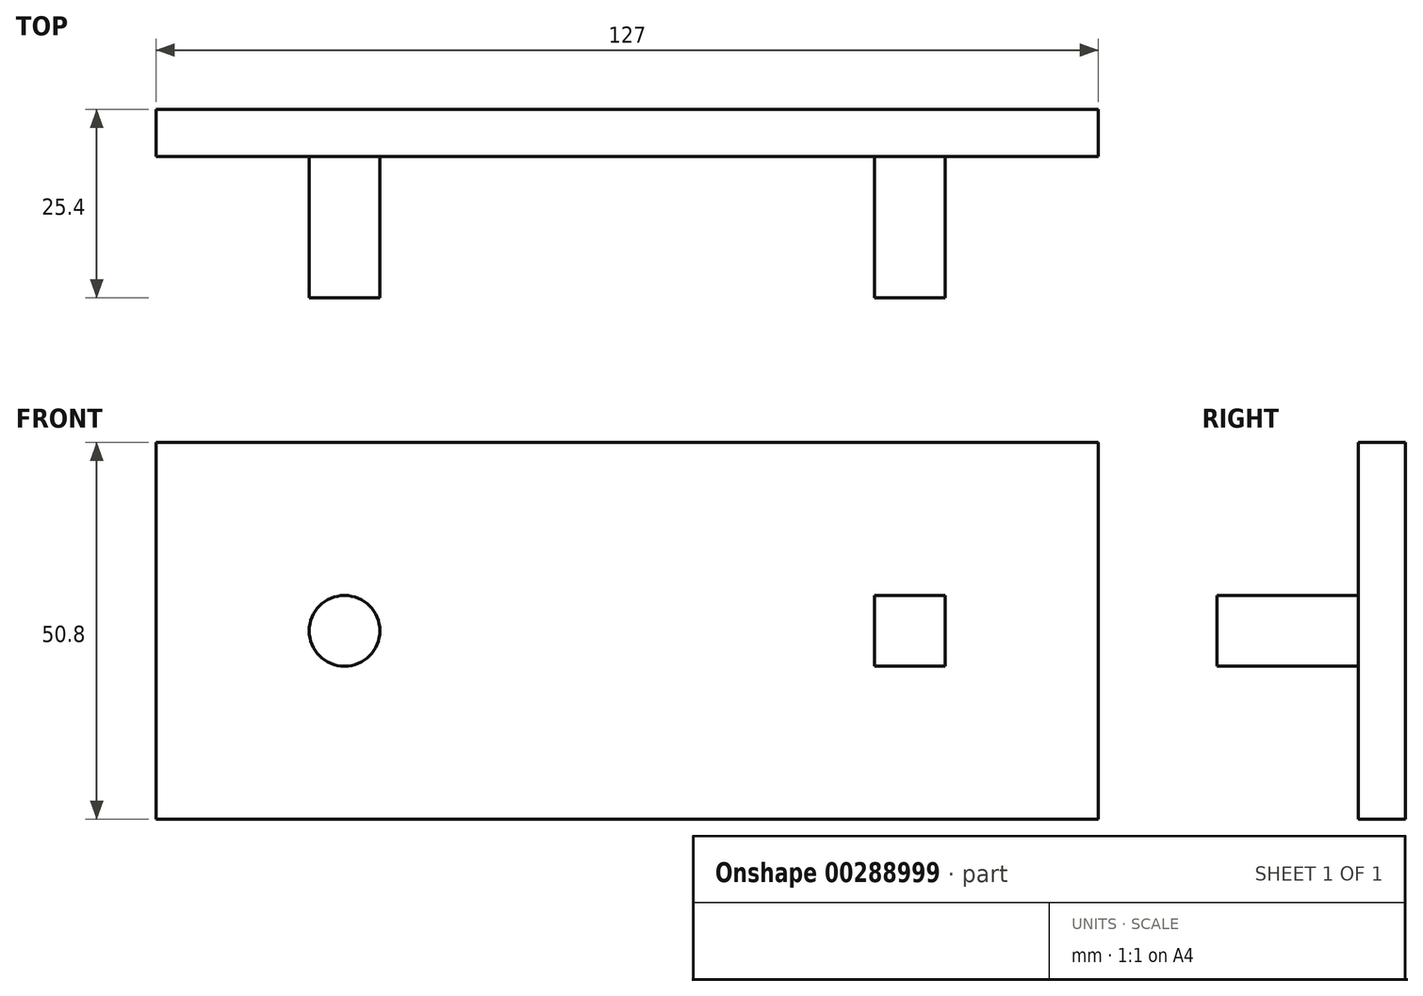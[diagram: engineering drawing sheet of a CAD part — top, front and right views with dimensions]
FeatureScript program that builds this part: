
annotation { "Feature Type Name" : "Feature", "Feature Type Description" : "" }
export const myFeature = defineFeature(function(context is Context, id is Id, definition is map)
    precondition{}
    {
        {
            var Q0;
            Q0=qCreatedBy(makeId("Front.planeOp"),FACE);
            var sketch = newSketch(context, id + "F0", { "sketchPlane" : qUnion([Q0])});
            skLineSegment(sketch, "E0.bottom", {"start": v(-63.5, 25.4) * mm, "end": v(63.5, 25.4) * mm});
            skLineSegment(sketch, "E0.top", {"start": v(-63.5, -25.4) * mm, "end": v(63.5, -25.4) * mm});
            skLineSegment(sketch, "E0.left", {"start": v(-63.5, 25.4) * mm, "end": v(-63.5, -25.4) * mm});
            skLineSegment(sketch, "E0.right", {"start": v(63.5, 25.4) * mm, "end": v(63.5, -25.4) * mm});
            skPoint(sketch, "E0.middle", {"position": v(0, 0) * mm});
            skPoint(sketch, "E1.endSnap0", {"position": v(-63.5, 0) * mm});
            skCircle(sketch, "E2", {"center": v(-38.1, 0) * mm, "radius": 4.76 * mm});
            skLineSegment(sketch, "E3.bottom", {"start": v(33.34, 4.76) * mm, "end": v(42.86, 4.76) * mm});
            skLineSegment(sketch, "E3.top", {"start": v(33.34, -4.76) * mm, "end": v(42.86, -4.76) * mm});
            skLineSegment(sketch, "E3.left", {"start": v(33.34, 4.76) * mm, "end": v(33.34, -4.76) * mm});
            skLineSegment(sketch, "E3.right", {"start": v(42.86, 4.76) * mm, "end": v(42.86, -4.76) * mm});
            skPoint(sketch, "E3.middle", {"position": v(38.1, 0) * mm});
            skSolve(sketch);
        }
        {
            var Q0;
            Q0=makeQuery(id+"F0.imprint","IMPRINT",FACE,{"disambiguationData":[TD([[makeQuery(id+"F0.imprint","IMPRINT",EDGE,{"derivedFrom":sQuery(id+"F0.wireOp",EDGE,"E0.bottom")}),-1.0]])]});
            var Q1;
            Q1=makeQuery(id+"F0.imprint","IMPRINT",FACE,{"disambiguationData":[TD([[makeQuery(id+"F0.imprint","IMPRINT",EDGE,{"derivedFrom":sQuery(id+"F0.wireOp",EDGE,"E3.bottom")}),-1.0]])]});
            var Q2;
            Q2=makeQuery(id+"F0.imprint","IMPRINT",FACE,{"disambiguationData":[TD([[makeQuery(id+"F0.imprint","IMPRINT",EDGE,{"derivedFrom":sQuery(id+"F0.wireOp",EDGE,"E2")}),1.0]])]});
            extrude(context, id + "F1", {"entities" : qUnion([Q0, Q1, Q2]), "oppositeDirection" : true, "depth" : 6.35 * mm});
        }
        {
            var Q0;
            Q0=makeQuery(id+"F0.imprint","IMPRINT",FACE,{"disambiguationData":[TD([[makeQuery(id+"F0.imprint","IMPRINT",EDGE,{"derivedFrom":sQuery(id+"F0.wireOp",EDGE,"E3.bottom")}),-1.0]])]});
            var Q1;
            Q1=makeQuery(id+"F0.imprint","IMPRINT",FACE,{"disambiguationData":[TD([[makeQuery(id+"F0.imprint","IMPRINT",EDGE,{"derivedFrom":sQuery(id+"F0.wireOp",EDGE,"E2")}),1.0]])]});
            extrude(context, id + "F2", {"entities" : qUnion([Q0, Q1]), "operationType" : NewBodyOperationType.ADD, "depth" : 19.05 * mm});
        }
    });
